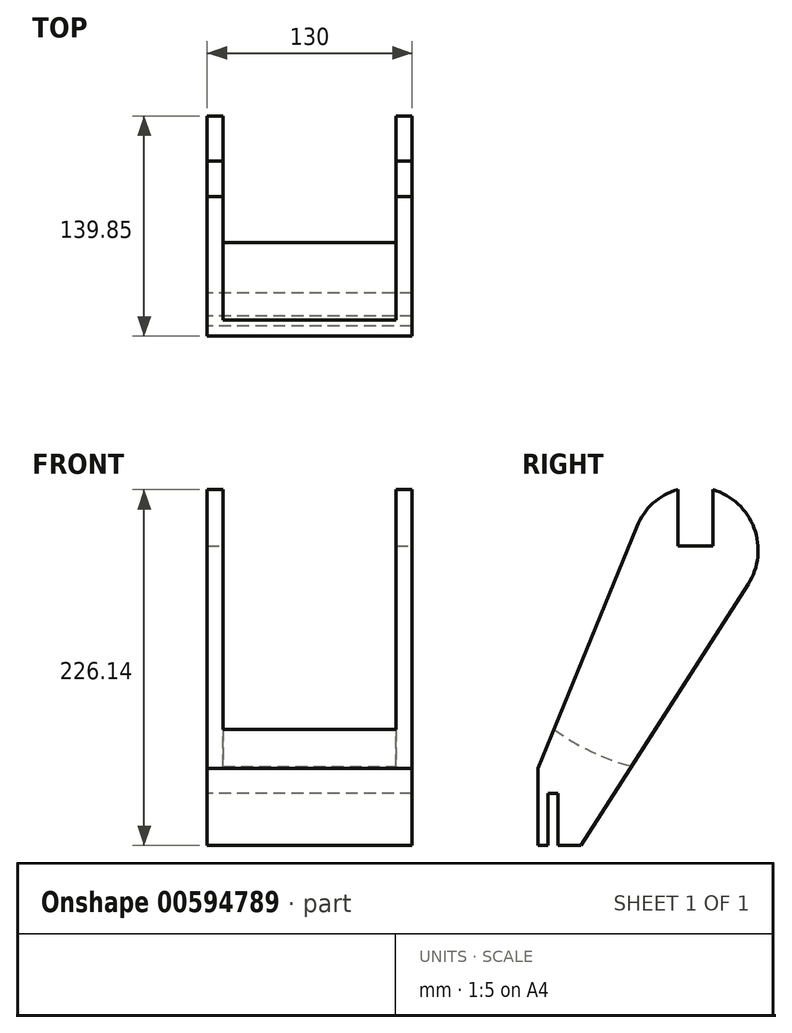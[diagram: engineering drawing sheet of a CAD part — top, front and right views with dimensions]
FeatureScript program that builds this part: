
annotation { "Feature Type Name" : "Feature", "Feature Type Description" : "" }
export const myFeature = defineFeature(function(context is Context, id is Id, definition is map)
    precondition{}
    {
        {
            var Q0;
            Q0=qCreatedBy(makeId("Right.planeOp"),FACE);
            var sketch = newSketch(context, id + "F0", { "sketchPlane" : qUnion([Q0])});
            skLineSegment(sketch, "E0", {"start": v(0, 0) * mm, "end": v(0, 49.1) * mm});
            skLineSegment(sketch, "E1", {"start": v(0, 49.1) * mm, "end": v(62.82, 202.84) * mm});
            skLineSegment(sketch, "E2", {"start": v(0, 0) * mm, "end": v(27.36, 0) * mm});
            skLineSegment(sketch, "E3", {"start": v(27.36, 0) * mm, "end": v(27.36, 0) * mm});
            skLineSegment(sketch, "E4", {"start": v(27.36, 0) * mm, "end": v(133.55, 166.16) * mm});
            skCircle(sketch, "E5", {"center": v(100, 200) * mm, "radius": 150 * mm, "construction": true});
            skCircle(sketch, "E6", {"center": v(100, 200) * mm, "radius": 26 * mm, "construction": true});
            skLineSegment(sketch, "E7.bottom", {"start": v(6.41, 0) * mm, "end": v(12.81, 0) * mm});
            skLineSegment(sketch, "E7.top", {"start": v(6.41, 33.17) * mm, "end": v(12.81, 33.17) * mm});
            skLineSegment(sketch, "E7.left", {"start": v(6.41, 0) * mm, "end": v(6.41, 33.17) * mm});
            skLineSegment(sketch, "E7.right", {"start": v(12.81, 0) * mm, "end": v(12.81, 33.17) * mm});
            skCircle(sketch, "E8", {"center": v(99.85, 187.7) * mm, "radius": 40 * mm});
            skSolve(sketch);
        }
        {
            var Q0;
            {var subQ4=sQuery(id+"F0.wireOp",EDGE,"E0");Q0=makeQuery(id+"F0.imprint","IMPRINT",FACE,{"disambiguationData":[TD([[makeQuery(id+"F0.imprint","IMPRINT",EDGE,{"derivedFrom":subQ4}),-1.0]])]});}
            var Q1;
            {var subQ0=sQuery(id+"F0.wireOp",EDGE,"E8");var subQ1=makeQuery(id+"F0.imprint","INTERSECT",VERTEX,{"derivedFrom":[sQuery(id+"F0.wireOp",EDGE,"E1"),subQ0]});Q1=makeQuery(id+"F0.imprint","IMPRINT",FACE,{"disambiguationData":[TD([[makeQuery(id+"F0.imprint","IMPRINT",EDGE,{"disambiguationData":[TD([[subQ1,-1.0]])],"derivedFrom":subQ0}),1.0]])]});}
            extrude(context, id + "F1", {"entities" : qUnion([Q0, Q1]), "endBound" : BoundingType.SYMMETRIC, "depth" : 130 * mm, "offsetDistance" : 25 * mm});
        }
        {
            var Q0;
            Q0=qCreatedBy(makeId("Right.planeOp"),FACE);
            var sketch = newSketch(context, id + "F2", { "sketchPlane" : qUnion([Q0])});
            skCircle(sketch, "E9", {"center": v(100, 200) * mm, "radius": 155 * mm});
            skSolve(sketch);
        }
        {
            var Q0;
            Q0 = qSketchRegion(id + "F2", true);
            extrude(context, id + "F3", {"entities" : qUnion([Q0]), "operationType" : NewBodyOperationType.REMOVE, "endBound" : BoundingType.SYMMETRIC, "oppositeDirection" : true, "depth" : 110 * mm, "offsetDistance" : 25 * mm});
        }
        {
            var Q0;
            Q0=qCreatedBy(makeId("Right.planeOp"),FACE);
            var sketch = newSketch(context, id + "F4", { "sketchPlane" : qUnion([Q0])});
            skLineSegment(sketch, "E10.bottom", {"start": v(88.77, 190.28) * mm, "end": v(111.23, 190.28) * mm});
            skLineSegment(sketch, "E10.top", {"start": v(88.77, 240.28) * mm, "end": v(111.23, 240.28) * mm});
            skLineSegment(sketch, "E10.left", {"start": v(88.77, 190.28) * mm, "end": v(88.77, 240.28) * mm});
            skLineSegment(sketch, "E10.right", {"start": v(111.23, 190.28) * mm, "end": v(111.23, 240.28) * mm});
            skPoint(sketch, "E10.middle", {"position": v(100, 215.28) * mm});
            skLineSegment(sketch, "E11", {"start": v(100, 215.28) * mm, "end": v(100, 200) * mm, "construction": true});
            skSolve(sketch);
        }
        {
            var Q0;
            Q0=makeQuery(id+"F4.imprint","IMPRINT",FACE,{"disambiguationData":[TD([[makeQuery(id+"F4.imprint","IMPRINT",EDGE,{"derivedFrom":sQuery(id+"F4.wireOp",EDGE,"E10.bottom")}),1.0]])]});
            extrude(context, id + "F5", {"entities" : qUnion([Q0]), "operationType" : NewBodyOperationType.REMOVE, "endBound" : BoundingType.THROUGH_ALL, "oppositeDirection" : true, "depth" : 25 * mm, "offsetDistance" : 25 * mm, "hasSecondDirection" : true, "secondDirectionBound" : SecondDirectionBoundingType.THROUGH_ALL, "secondDirectionOppositeDirection" : false, "secondDirectionDepth" : 25 * mm});
        }
    });
